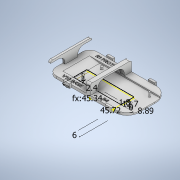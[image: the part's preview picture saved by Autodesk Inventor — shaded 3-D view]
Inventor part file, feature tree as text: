
AUTODESK INVENTOR PART (.ipt)
format: ipt  version: 2021 (Build 250183000, 183)  size: 1,734,144 bytes
history: native  units: in
note: dims shown in document units (in); Inventor stores cm internally (conversion verified against a paired STEP export)
features: extrude x12, sketch x11, fillet x6, mirror x3, plane x2, chamfer x1
ambient origin geometry x8: Origin, YZ Plane, XZ Plane, XY Plane, X Axis, Y Axis, Z Axis, Center Point
bodies: Solid1 (feature_tree)
feature tree (35):
  extrude  "Extrusion1"  Depth=0.7756in
  extrude  "Extrusion2"  Depth=0.2362in
  plane  "Work Plane1"
  extrude  "Extrusion3"  Depth=0.2362in
  sketch  "Sketch5"  dims[d14=1.3386in d15=0.0in]
  extrude  "Extrusion4"  TaperAngle=0.0deg  [1 undecoded]
  sketch  "Sketch7"  dims[d19=0.8661in d20=0.374in d21=0.0in d22=0.7756in]
  extrude  "Extrusion5"  Depth=0.1575in
  plane  "Work Plane2"
  extrude  "Extrusion8"  Depth=0.374in
  fillet  "Fillet3"  [1 undecoded]
  fillet  "Fillet4"  Radius=0.7756in
  sketch  "Sketch13"  dims[d26=1.4803in]
  extrude  "Extrusion9"  Depth=0.5in
  mirror  "Mirror3"
  chamfer  "Chamfer1"  Distance=0.748in
  extrude  "Extrusion11"  Depth=0.5in
  extrude  "Extrusion13"  Depth=0.0472in TaperAngle=0.0deg
  mirror  "Mirror4"
  extrude  "Extrusion14"  Depth=0.0787in
  extrude  "Extrusion15"  Depth=0.2756in
  mirror  "Mirror5"
  fillet  "Fillet8"  Radius=0.0709in
  fillet  "Fillet9"  Radius=0.0945in
  fillet  "Fillet10"  Radius=1.8in
  extrude  "Extrusion17"  Depth=0.35in
  fillet  "Fillet11"  Radius=0.1575in
  sketch  "Sketch1"  dims[d5=2.4409in d6=0.7756in]
  sketch  "Sketch3"  dims[d7=0.0945in d8=0.0in d9=0.2362in]
  sketch  "Sketch4"  dims[d10=0.0787in d11=0.0in d13=0.2362in]
  sketch  "Sketch6"  dims[d16=0.063in d17=0.0in d18=0.1575in]
  sketch  "Sketch8"  dims[d23=0.374in d24=0.5in]
  sketch  "Sketch12"  dims[d25=0.315in]
  sketch  "Sketch18"  dims[d27=0.0in d29=-0.748in d30=0.748in]
  sketch  "Sketch19"  dims[d41=1.785in d42=0.5in d43=0.0472in d44=0.0in d46=0.0787in d47=0.2756in d48=0.0709in d49=0.0945in d50=1.8in d51=0.35in d52=0.1575in d53=0.0in d56=0.3937in d57=0.0472in d58=45.0deg d59=0.0787in d60=0.0787in d61=0.0394in d64=0.0394in d66=0.0787in d67=0.0394in d68=0.0in d69=0.0in d70=0.0in d71=0.2397in d72=0.2397in d74=0.315in d76=0.2362in d77=0.0787in d78=0.0in d79=0.0945in d84=0.2953in d85=0.0in d86=0.0in d87=0.0787in d90=0.0787in d91=0.7756in d92=0.0787in d93=0.0in d96=0.0in d97=0.2362in d98=0.2756in d99=0.0787in d100=0.0in d101=0.315in d104=0.0472in d105=0.0472in d106=0.5118in d107=0.0in d108=0.5118in d102=0.0197in d103=0.0344in]
note: 2 required parameter values undecoded (feature->parameter linkage not recoverable at this tier; creation-order binding heuristic only, values carry confidence <= 0.55)
